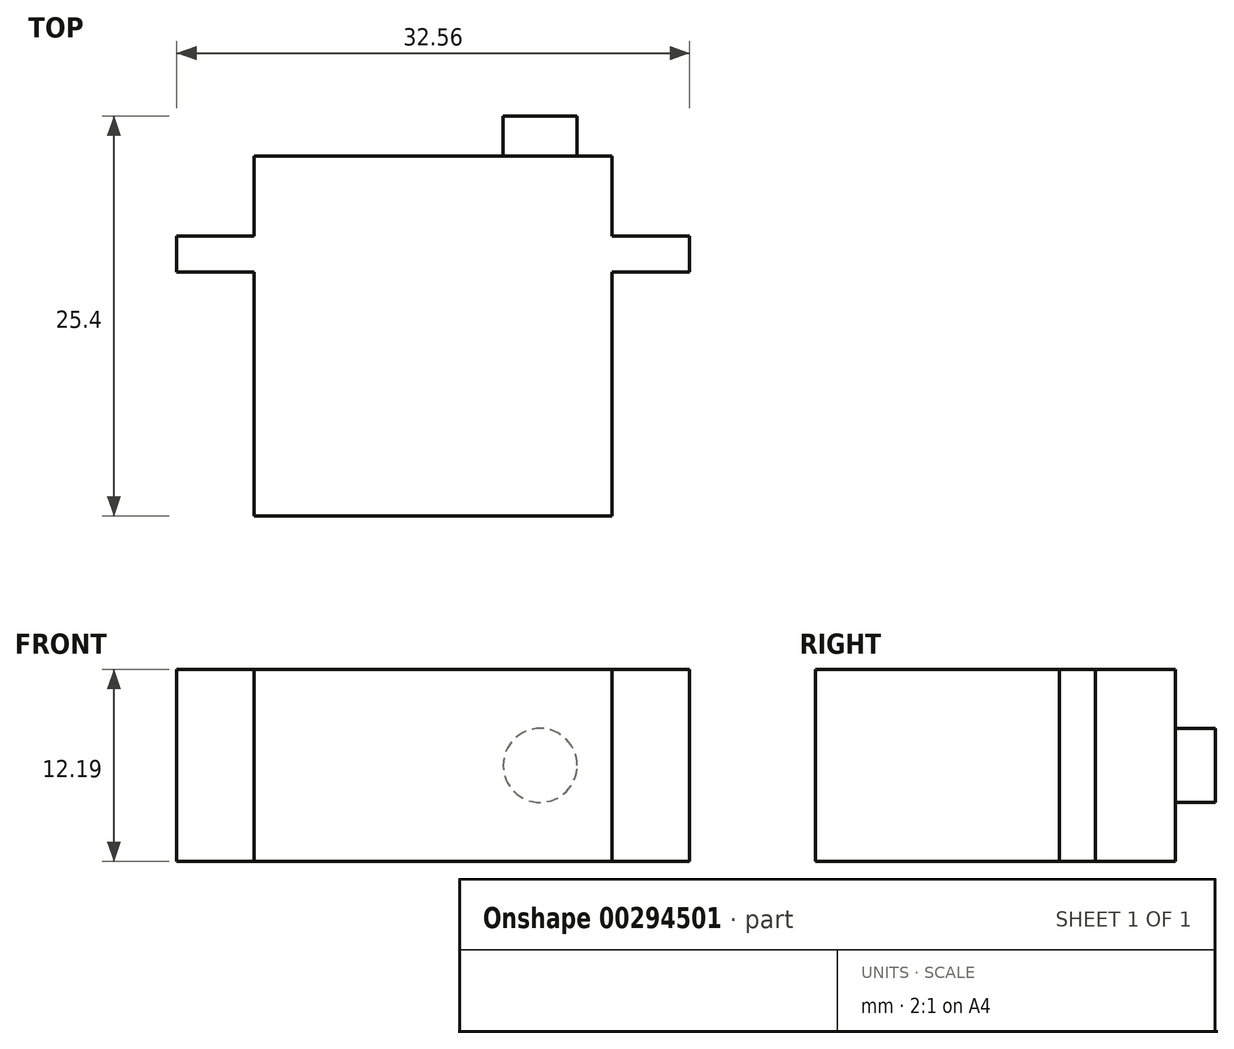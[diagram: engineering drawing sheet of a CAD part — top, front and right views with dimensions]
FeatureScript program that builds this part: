
annotation { "Feature Type Name" : "Feature", "Feature Type Description" : "" }
export const myFeature = defineFeature(function(context is Context, id is Id, definition is map)
    precondition{}
    {
        {
            var Q0;
            Q0=qCreatedBy(makeId("Top.planeOp"),FACE);
            var sketch = newSketch(context, id + "F0", { "sketchPlane" : qUnion([Q0])});
            skLineSegment(sketch, "E0.bottom", {"start": v(11.37, 11.43) * mm, "end": v(-11.37, 11.43) * mm});
            skLineSegment(sketch, "E0.top", {"start": v(11.37, -11.43) * mm, "end": v(-11.37, -11.43) * mm});
            skLineSegment(sketch, "E0.left", {"start": v(11.37, 11.43) * mm, "end": v(11.37, -11.43) * mm});
            skLineSegment(sketch, "E0.right", {"start": v(-11.37, 11.43) * mm, "end": v(-11.37, -11.43) * mm});
            skPoint(sketch, "E0.middle", {"position": v(0, 0) * mm});
            skLineSegment(sketch, "E1.bottom", {"start": v(16.28, 6.35) * mm, "end": v(-16.28, 6.35) * mm});
            skLineSegment(sketch, "E1.top", {"start": v(16.28, 4.06) * mm, "end": v(-16.28, 4.06) * mm});
            skLineSegment(sketch, "E1.left", {"start": v(16.28, 6.35) * mm, "end": v(16.28, 4.06) * mm});
            skLineSegment(sketch, "E1.right", {"start": v(-16.28, 6.35) * mm, "end": v(-16.28, 4.06) * mm});
            skPoint(sketch, "E1.middle", {"position": v(0, 5.2) * mm});
            skSolve(sketch);
        }
        {
            var Q0;
            {var subQ0=sQuery(id+"F0.wireOp",EDGE,"E0.bottom");Q0=makeQuery(id+"F0.imprint","IMPRINT",FACE,{"disambiguationData":[TD([[makeQuery(id+"F0.imprint","IMPRINT",EDGE,{"derivedFrom":subQ0}),1.0]])]});}
            var Q1;
            {var subQ0=sQuery(id+"F0.wireOp",EDGE,"E1.bottom");var subQ1=sQuery(id+"F0.wireOp",EDGE,"E0.left");var subQ2=makeQuery(id+"F0.imprint","INTERSECT",VERTEX,{"derivedFrom":[subQ1,subQ0]});Q1=makeQuery(id+"F0.imprint","IMPRINT",FACE,{"disambiguationData":[TD([[makeQuery(id+"F0.imprint","IMPRINT",EDGE,{"disambiguationData":[TD([[subQ2,-1.0]])],"derivedFrom":subQ1}),-1.0]])]});}
            var Q2;
            {var subQ5=sQuery(id+"F0.wireOp",EDGE,"E1.right");Q2=makeQuery(id+"F0.imprint","IMPRINT",FACE,{"disambiguationData":[TD([[makeQuery(id+"F0.imprint","IMPRINT",EDGE,{"derivedFrom":subQ5}),1.0]])]});}
            var Q3;
            {var subQ0=sQuery(id+"F0.wireOp",EDGE,"E0.top");Q3=makeQuery(id+"F0.imprint","IMPRINT",FACE,{"disambiguationData":[TD([[makeQuery(id+"F0.imprint","IMPRINT",EDGE,{"derivedFrom":subQ0}),-1.0]])]});}
            var Q4;
            {var subQ5=sQuery(id+"F0.wireOp",EDGE,"E1.left");Q4=makeQuery(id+"F0.imprint","IMPRINT",FACE,{"disambiguationData":[TD([[makeQuery(id+"F0.imprint","IMPRINT",EDGE,{"derivedFrom":subQ5}),-1.0]])]});}
            extrude(context, id + "F1", {"entities" : qUnion([Q0, Q1, Q2, Q3, Q4]), "depth" : 12.2 * mm});
        }
        {
            var Q0;
            Q0=makeQuery(id+"F1.opExtrude","SWEPT_FACE",FACE,{"disambiguationData":[OSD([sQuery(id+"F0.wireOp",EDGE,"E0.bottom")])]});
            var sketch = newSketch(context, id + "F2", { "sketchPlane" : qUnion([Q0])});
            skCircle(sketch, "E2", {"center": v(-6.8, 6.1) * mm, "radius": 2.35 * mm});
            skPoint(sketch, "E2.centerSnap0", {"position": v(-11.37, 6.1) * mm});
            skSolve(sketch);
        }
        {
            var Q0;
            Q0=makeQuery(id+"F2.imprint","IMPRINT",FACE,{"disambiguationData":[TD([[makeQuery(id+"F2.imprint","IMPRINT",EDGE,{"derivedFrom":sQuery(id+"F2.wireOp",EDGE,"E2")}),1.0]])]});
            extrude(context, id + "F3", {"entities" : qUnion([Q0]), "operationType" : NewBodyOperationType.ADD, "depth" : 2.54 * mm});
        }
    });
